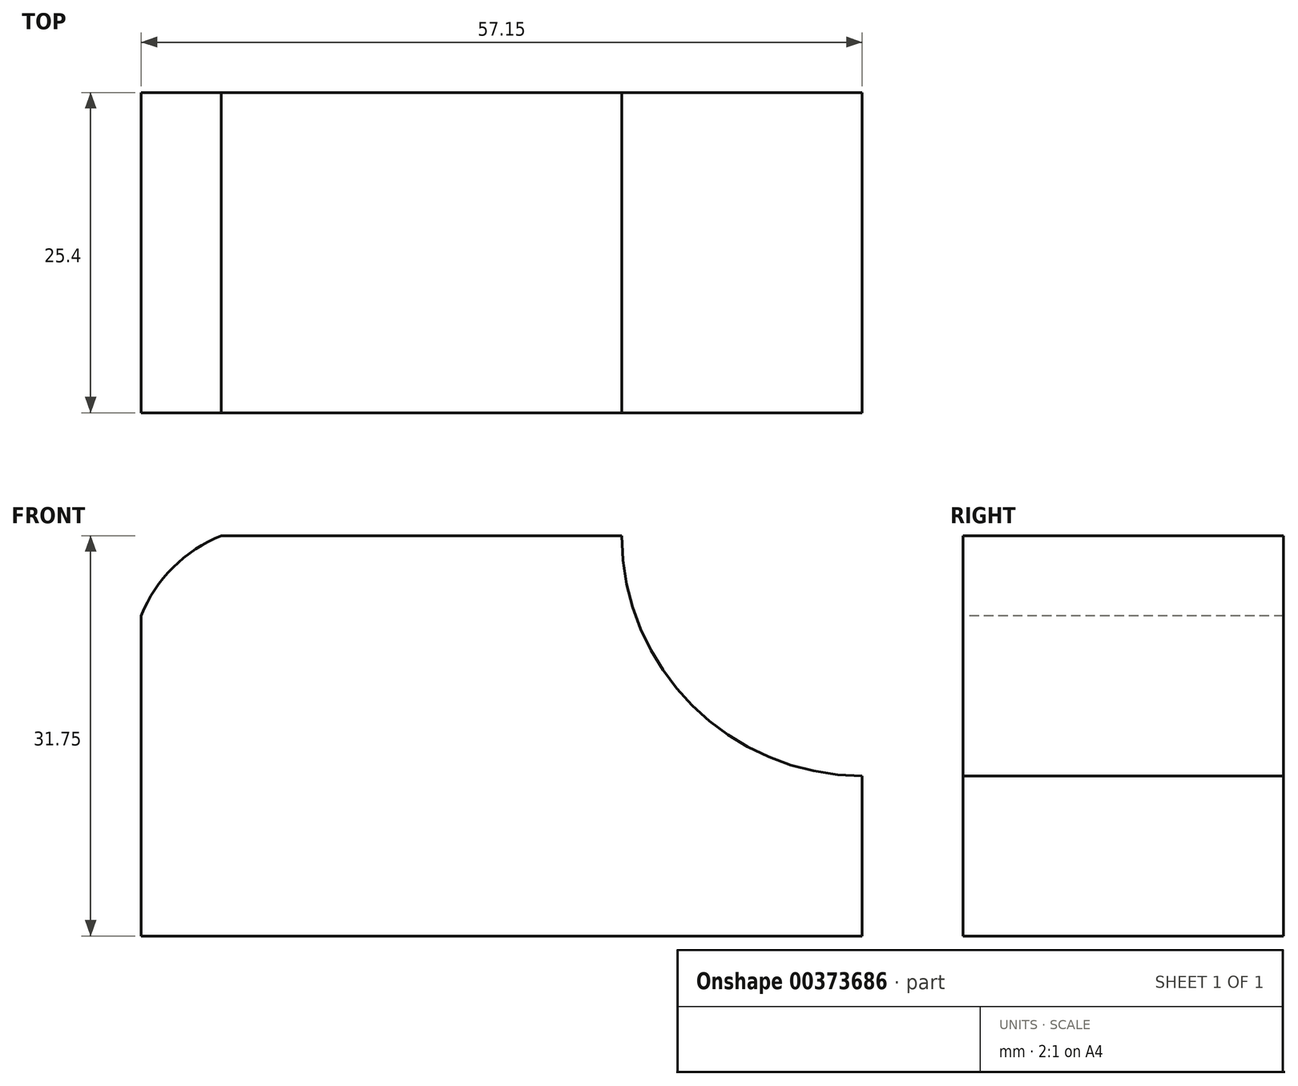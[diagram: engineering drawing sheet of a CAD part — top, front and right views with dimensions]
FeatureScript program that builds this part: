
annotation { "Feature Type Name" : "Feature", "Feature Type Description" : "" }
export const myFeature = defineFeature(function(context is Context, id is Id, definition is map)
    precondition{}
    {
        {
            var Q0;
            Q0=qCreatedBy(makeId("Front.planeOp"),FACE);
            var sketch = newSketch(context, id + "F0", { "sketchPlane" : qUnion([Q0])});
            skLineSegment(sketch, "E0", {"start": v(57.15, 0) * mm, "end": v(57.15, 31.75) * mm});
            skLineSegment(sketch, "E1", {"start": v(57.15, 31.75) * mm, "end": v(0, 31.75) * mm});
            skLineSegment(sketch, "E2", {"start": v(0, 31.75) * mm, "end": v(0, 0) * mm});
            skLineSegment(sketch, "E3", {"start": v(0, 0) * mm, "end": v(57.15, 0) * mm});
            skSolve(sketch);
        }
        {
            var Q0;
            Q0 = qSketchRegion(id + "F0", true);
            extrude(context, id + "F1", {"entities" : qUnion([Q0]), "depth" : 25.4 * mm});
        }
        {
            var Q0;
            Q0=makeQuery(id+"F1.opExtrude","CAP_FACE",FACE,{"disambiguationData":[OSD([sQuery(id+"F0.wireOp",EDGE,"E0"),sQuery(id+"F0.wireOp",EDGE,"E1"),sQuery(id+"F0.wireOp",EDGE,"E2"),sQuery(id+"F0.wireOp",EDGE,"E3")])],"isStart":false});
            var sketch = newSketch(context, id + "F2", { "sketchPlane" : qUnion([Q0])});
            skCircle(sketch, "E4", {"center": v(57.15, 31.75) * mm, "radius": 19.05 * mm});
            skArc(sketch, "E5", {"start": v(6.35, 31.75) * mm, "mid": v(2.52, 29.23) * mm, "end": v(0, 25.4) * mm});
            skSolve(sketch);
        }
        {
            var Q0;
            {var subQ0=sQuery(id+"F2.wireOp",EDGE,"E4");var subQ1=makeQuery(id+"F1.opExtrude","CAP_EDGE",EDGE,{"disambiguationData":[OSD([sQuery(id+"F0.wireOp",EDGE,"E0")])],"isStart":false});var subQ2=makeQuery(id+"F2.imprint","INTERSECT",VERTEX,{"derivedFrom":[subQ1,subQ0]});Q0=makeQuery(id+"F2.imprint","IMPRINT",FACE,{"disambiguationData":[TD([[makeQuery(id+"F2.imprint","IMPRINT",EDGE,{"disambiguationData":[TD([[subQ2,1.0]])],"derivedFrom":subQ0}),1.0]])]});}
            var Q1;
            {var subQ0=sQuery(id+"F2.wireOp",EDGE,"E5");Q1=makeQuery(id+"F2.imprint","IMPRINT",FACE,{"disambiguationData":[TD([[makeQuery(id+"F2.imprint","IMPRINT",EDGE,{"derivedFrom":subQ0}),-1.0]])]});}
            extrude(context, id + "F3", {"entities" : qUnion([Q0, Q1]), "operationType" : NewBodyOperationType.REMOVE, "oppositeDirection" : true, "depth" : 25.4 * mm});
        }
    });
